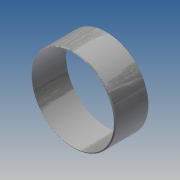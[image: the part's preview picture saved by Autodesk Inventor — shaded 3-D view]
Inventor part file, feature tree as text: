
AUTODESK INVENTOR PART (.ipt)
format: ipt  version: 2017.3 (Build 213257000, 257)  size: 99,328 bytes
history: native  units: in
note: dims shown in document units (in); Inventor stores cm internally (conversion verified against a paired STEP export)
features: chamfer x2, extrude x1, sketch x1
ambient origin geometry x8: Origin, YZ Plane, XZ Plane, XY Plane, X Axis, Y Axis, Z Axis, Center Point
bodies: Solid1 (feature_tree)
feature tree (4):
  extrude  "Extrusion1"  Depth=14.529in
  chamfer  "Chamfer1"  Distance=14.529in
  chamfer  "Chamfer2"  Distance=0.4375in
  sketch  "Sketch1"  dims[d0=36.0in d1=35.0in d2=14.529in d3=0.0in d4=0.4375in d5=0.125in d6=0.2577in d7=0.4375in d8=0.125in d9=0.2577in]
